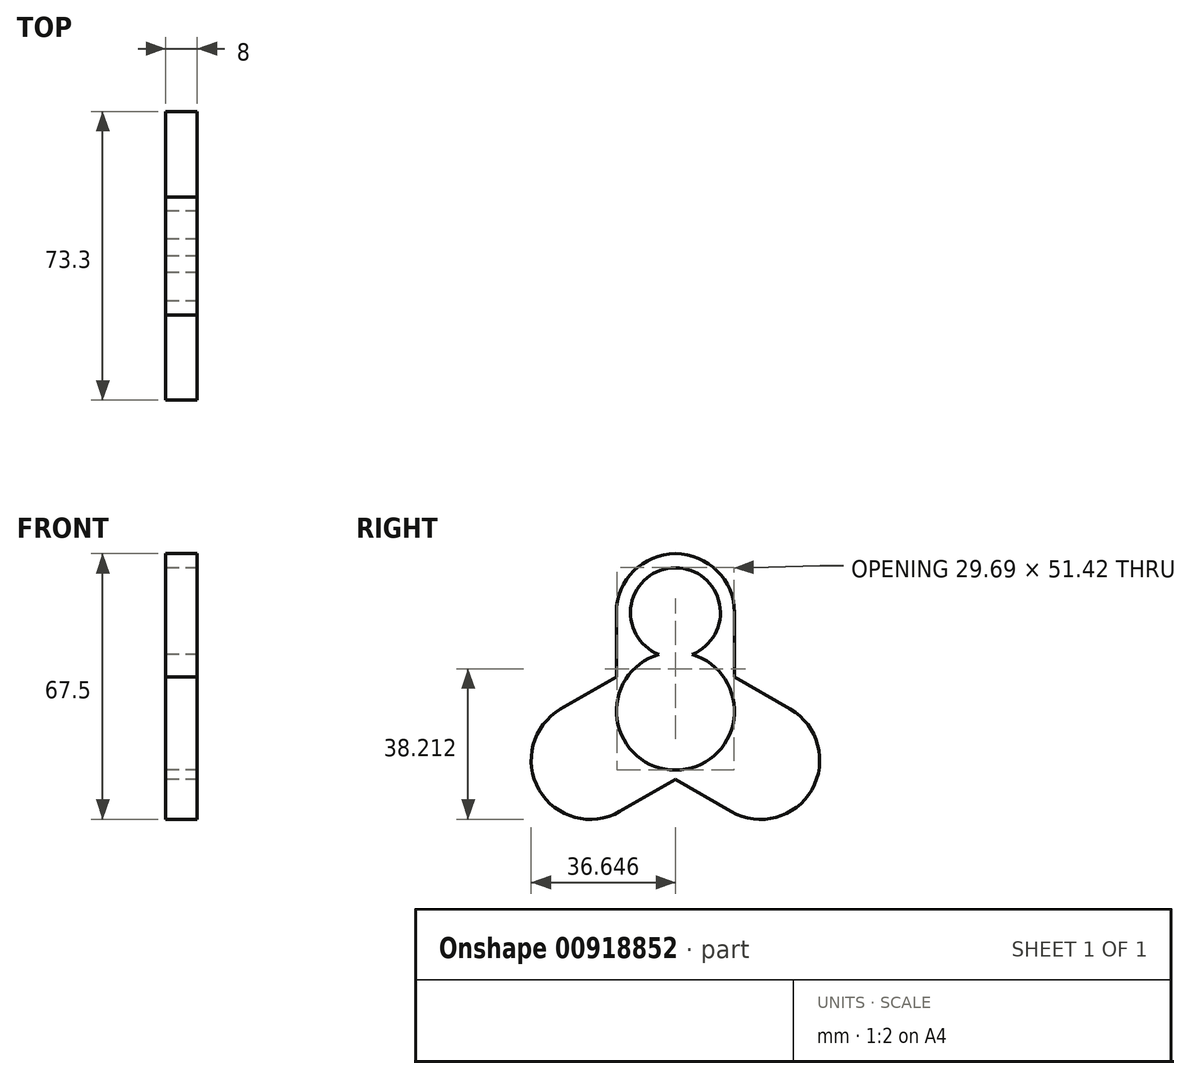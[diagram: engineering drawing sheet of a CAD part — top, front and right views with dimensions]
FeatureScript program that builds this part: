
annotation { "Feature Type Name" : "Feature", "Feature Type Description" : "" }
export const myFeature = defineFeature(function(context is Context, id is Id, definition is map)
    precondition{}
    {
        {
            var Q0;
            Q0=qCreatedBy(makeId("Right.planeOp"),FACE);
            var sketch = newSketch(context, id + "F0", { "sketchPlane" : qUnion([Q0])});
            skCircle(sketch, "E0", {"center": v(-204.7, 0) * mm, "radius": 11.42 * mm});
            skCircle(sketch, "E1", {"center": v(-204.7, 25) * mm, "radius": 11.43 * mm});
            skArc(sketch, "E2", {"start": v(-219.7, 25) * mm, "mid": v(-204.7, 40) * mm, "end": v(-189.7, 25) * mm});
            skArc(sketch, "E3", {"start": v(-189.7, 0) * mm, "mid": v(-204.7, -15) * mm, "end": v(-219.7, 0) * mm});
            skLineSegment(sketch, "E4", {"start": v(-189.7, 25) * mm, "end": v(-189.7, 0) * mm});
            skLineSegment(sketch, "E5", {"start": v(-219.7, 25) * mm, "end": v(-219.7, 0) * mm});
            skArc(sketch, "E6.1.1", {"start": v(-218.85, -25.5) * mm, "mid": v(-239.34, -20) * mm, "end": v(-233.85, 0.5) * mm});
            skLineSegment(sketch, "E6.1.2", {"start": v(-233.85, 0.5) * mm, "end": v(-212.2, 13) * mm});
            skArc(sketch, "E6.1.3", {"start": v(-212.2, 13) * mm, "mid": v(-191.71, 7.5) * mm, "end": v(-197.2, -13) * mm});
            skCircle(sketch, "E6.1.4", {"center": v(-226.35, -12.5) * mm, "radius": 11.43 * mm});
            skLineSegment(sketch, "E6.1.5", {"start": v(-218.85, -25.5) * mm, "end": v(-197.2, -13) * mm});
            skArc(sketch, "E6.2.1", {"start": v(-175.55, 0.5) * mm, "mid": v(-170.06, -20) * mm, "end": v(-190.55, -25.5) * mm});
            skLineSegment(sketch, "E6.2.2", {"start": v(-190.55, -25.5) * mm, "end": v(-212.2, -13) * mm});
            skArc(sketch, "E6.2.3", {"start": v(-212.2, -13) * mm, "mid": v(-217.7, 7.5) * mm, "end": v(-197.2, 13) * mm});
            skCircle(sketch, "E6.2.4", {"center": v(-183.05, -12.5) * mm, "radius": 11.43 * mm});
            skLineSegment(sketch, "E6.2.5", {"start": v(-175.55, 0.5) * mm, "end": v(-197.2, 13) * mm});
            skSolve(sketch);
        }
        {
            var Q0;
            Q0 = qSketchRegion(id + "F0", true);
            var Q1;
            {var subQ3=sQuery(id+"F0.wireOp",EDGE,"E3");Q1=makeQuery(id+"F0.imprint","IMPRINT",FACE,{"disambiguationData":[TD([[makeQuery(id+"F0.imprint","IMPRINT",EDGE,{"derivedFrom":subQ3}),-1.0]])]});}
            extrude(context, id + "F1", {"entities" : qUnion([Q0, Q1]), "depth" : 8 * mm, "offsetDistance" : 25 * mm});
        }
    });
